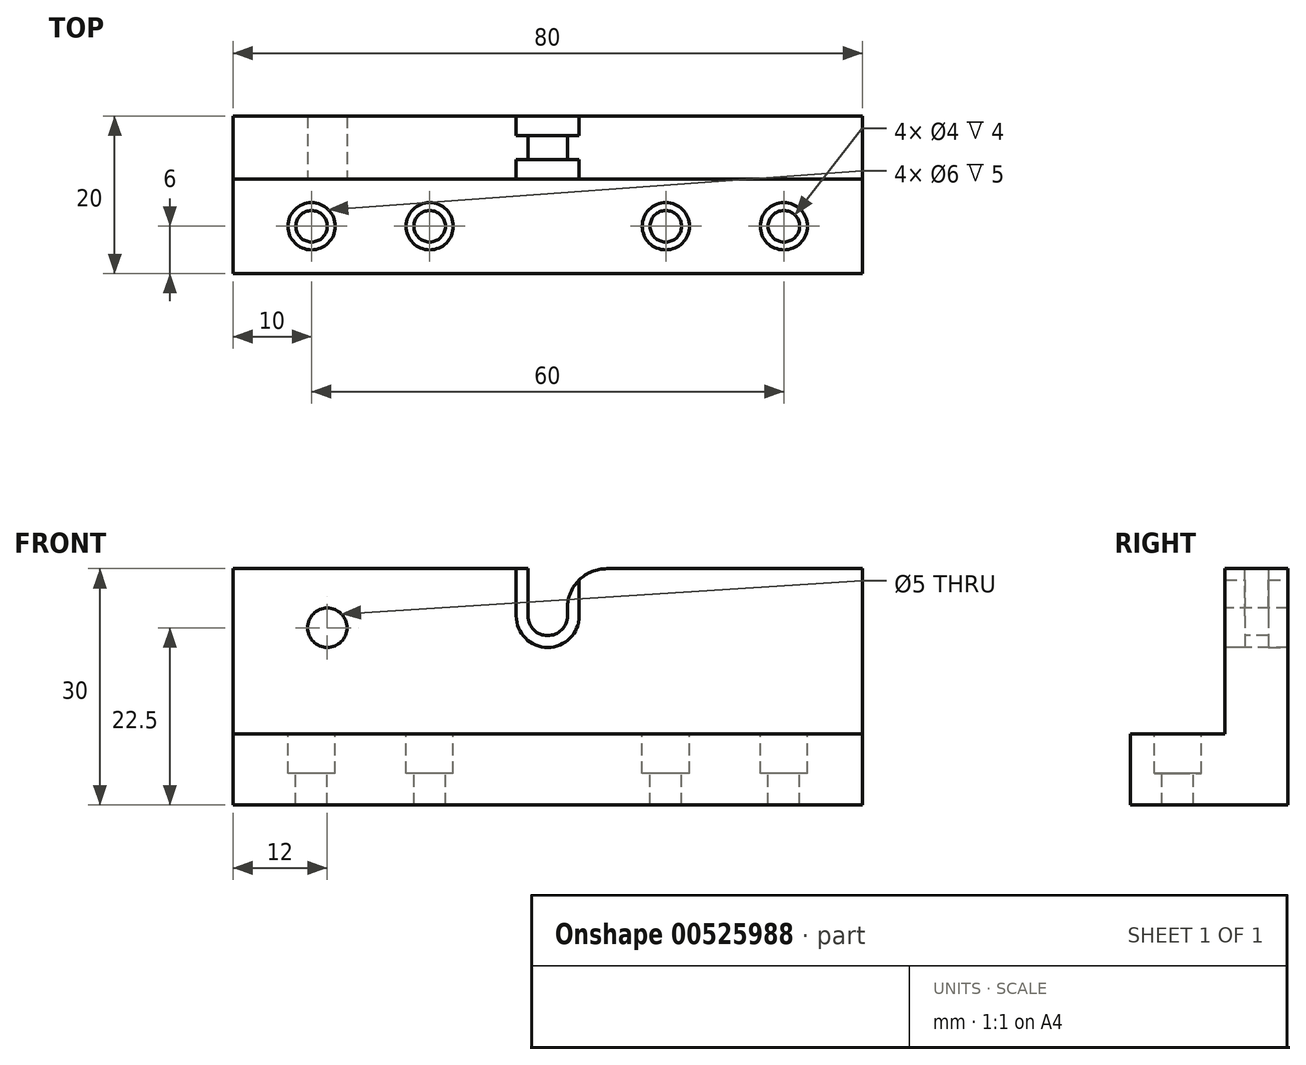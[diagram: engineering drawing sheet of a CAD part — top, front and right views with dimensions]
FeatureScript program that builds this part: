
annotation { "Feature Type Name" : "Feature", "Feature Type Description" : "" }
export const myFeature = defineFeature(function(context is Context, id is Id, definition is map)
    precondition{}
    {
        {
            var Q0;
            Q0=qCreatedBy(makeId("Top.planeOp"),FACE);
            var sketch = newSketch(context, id + "F0", { "sketchPlane" : qUnion([Q0])});
            skLineSegment(sketch, "E0.bottom", {"start": v(0, 0) * mm, "end": v(80, 0) * mm});
            skLineSegment(sketch, "E0.top", {"start": v(0, 8) * mm, "end": v(80, 8) * mm});
            skLineSegment(sketch, "E0.left", {"start": v(0, 0) * mm, "end": v(0, 8) * mm});
            skLineSegment(sketch, "E0.right", {"start": v(80, 0) * mm, "end": v(80, 8) * mm});
            skSolve(sketch);
        }
        {
            var Q0;
            Q0 = qSketchRegion(id + "F0", true);
            extrude(context, id + "F1", {"entities" : qUnion([Q0]), "depth" : 21 * mm, "offsetDistance" : 25 * mm});
        }
        {
            var Q0;
            Q0=makeQuery(id+"F1.opExtrude","SWEPT_FACE",FACE,{"disambiguationData":[OSD([sQuery(id+"F0.wireOp",EDGE,"E0.bottom")])]});
            var sketch = newSketch(context, id + "F2", { "sketchPlane" : qUnion([Q0])});
            skLineSegment(sketch, "E1", {"start": v(40, 21) * mm, "end": v(40, 0) * mm, "construction": true});
            skArc(sketch, "E2", {"start": v(37.5, 15) * mm, "mid": v(40, 12.5) * mm, "end": v(42.5, 15) * mm});
            skLineSegment(sketch, "E3", {"start": v(42.5, 15) * mm, "end": v(42.5, 21) * mm});
            skLineSegment(sketch, "E4", {"start": v(37.5, 15) * mm, "end": v(37.5, 21) * mm});
            skLineSegment(sketch, "E5", {"start": v(37.5, 21) * mm, "end": v(42.5, 21) * mm});
            skLineSegment(sketch, "E6", {"start": v(80, 15) * mm, "end": v(0, 15) * mm, "construction": true});
            skSolve(sketch);
        }
        {
            var Q0;
            Q0 = qSketchRegion(id + "F2", true);
            extrude(context, id + "F3", {"entities" : qUnion([Q0]), "operationType" : NewBodyOperationType.REMOVE, "oppositeDirection" : true, "depth" : 25 * mm, "offsetDistance" : 25 * mm});
        }
        {
            var Q0;
            Q0=makeQuery(id+"F1.opExtrude","SWEPT_FACE",FACE,{"disambiguationData":[OSD([sQuery(id+"F0.wireOp",EDGE,"E0.bottom")])]});
            var sketch = newSketch(context, id + "F4", { "sketchPlane" : qUnion([Q0])});
            skLineSegment(sketch, "E7.0", {"start": v(36, 15) * mm, "end": v(36, 15) * mm});
            skArc(sketch, "E7.1", {"start": v(36, 15) * mm, "mid": v(40, 11) * mm, "end": v(44, 15) * mm});
            skLineSegment(sketch, "E7.2", {"start": v(44, 15) * mm, "end": v(44, 15) * mm});
            skLineSegment(sketch, "E8", {"start": v(36, 15) * mm, "end": v(36, 21) * mm});
            skLineSegment(sketch, "E9", {"start": v(44, 15) * mm, "end": v(44, 21) * mm});
            skLineSegment(sketch, "E10", {"start": v(36, 21) * mm, "end": v(44, 21) * mm});
            skSolve(sketch);
        }
        {
            var Q0;
            Q0=makeQuery(id+"F4.imprint","IMPRINT",FACE,{"disambiguationData":[TD([[makeQuery(id+"F4.imprint","IMPRINT",EDGE,{"derivedFrom":sQuery(id+"F4.wireOp",EDGE,"E7.1")}),1.0]])]});
            extrude(context, id + "F5", {"entities" : qUnion([Q0]), "operationType" : NewBodyOperationType.REMOVE, "oppositeDirection" : true, "depth" : 2.5 * mm, "offsetDistance" : 25 * mm});
        }
        {
            var Q0;
            Q0=makeQuery(id+"F1.opExtrude","SWEPT_FACE",FACE,{"disambiguationData":[OSD([sQuery(id+"F0.wireOp",EDGE,"E0.top")])]});
            var sketch = newSketch(context, id + "F6", { "sketchPlane" : qUnion([Q0])});
            skLineSegment(sketch, "E11.0", {"start": v(-44, 15) * mm, "end": v(-44, 15) * mm});
            skArc(sketch, "E11.1", {"start": v(-44, 15) * mm, "mid": v(-40, 11) * mm, "end": v(-36, 15) * mm});
            skLineSegment(sketch, "E11.2", {"start": v(-36, 15) * mm, "end": v(-36, 15) * mm});
            skLineSegment(sketch, "E12", {"start": v(-36, 15) * mm, "end": v(-36, 21) * mm});
            skLineSegment(sketch, "E13", {"start": v(-36, 21) * mm, "end": v(-44, 21) * mm});
            skLineSegment(sketch, "E14", {"start": v(-44, 21) * mm, "end": v(-44, 15) * mm});
            skSolve(sketch);
        }
        {
            var Q0;
            Q0=makeQuery(id+"F6.imprint","IMPRINT",FACE,{"disambiguationData":[TD([[makeQuery(id+"F6.imprint","IMPRINT",EDGE,{"derivedFrom":sQuery(id+"F6.wireOp",EDGE,"E11.1")}),1.0]])]});
            extrude(context, id + "F7", {"entities" : qUnion([Q0]), "operationType" : NewBodyOperationType.REMOVE, "oppositeDirection" : true, "depth" : 2.5 * mm, "offsetDistance" : 25 * mm});
        }
        {
            var Q0;
            Q0=makeQuery(id+"F3.boolean.opBoolean","COPY",EDGE,{"derivedFrom":makeQuery(id+"F3.opExtrude","SWEPT_EDGE",EDGE,{"disambiguationData":[OSD([sQuery(id+"F0.wireOp",EDGE,"E0.bottom"),sQuery(id+"F2.wireOp",EDGE,"E3"),sQuery(id+"F2.wireOp",EDGE,"E5")])]})});
            var Q1;
            Q1=makeQuery(id+"F3.boolean.opBoolean","COPY",EDGE,{"derivedFrom":makeQuery(id+"F3.opExtrude","SWEPT_EDGE",EDGE,{"disambiguationData":[OSD([sQuery(id+"F0.wireOp",EDGE,"E0.bottom"),sQuery(id+"F2.wireOp",EDGE,"E4"),sQuery(id+"F2.wireOp",EDGE,"E5")])]})});
            fillet(context, id + "F8", {"entities" : qUnion([Q0, Q1]), "radius" : 5 * mm, "tangentPropagation" : true, "allowEdgeOverflow" : false});
        }
        {
            var Q0;
            Q0=makeQuery(id+"F1.opExtrude","CAP_FACE",FACE,{"disambiguationData":[OSD([sQuery(id+"F0.wireOp",EDGE,"E0.bottom"),sQuery(id+"F0.wireOp",EDGE,"E0.top"),sQuery(id+"F0.wireOp",EDGE,"E0.left"),sQuery(id+"F0.wireOp",EDGE,"E0.right")])],"isStart":true});
            var sketch = newSketch(context, id + "F9", { "sketchPlane" : qUnion([Q0])});
            skLineSegment(sketch, "E15.bottom", {"start": v(80, -8) * mm, "end": v(0, -8) * mm});
            skLineSegment(sketch, "E15.top", {"start": v(80, 12) * mm, "end": v(0, 12) * mm});
            skLineSegment(sketch, "E15.left", {"start": v(80, -8) * mm, "end": v(80, 12) * mm});
            skLineSegment(sketch, "E15.right", {"start": v(0, -8) * mm, "end": v(0, 12) * mm});
            skSolve(sketch);
        }
        {
            var Q0;
            Q0 = qSketchRegion(id + "F9", true);
            extrude(context, id + "F10", {"entities" : qUnion([Q0]), "operationType" : NewBodyOperationType.ADD, "depth" : 9 * mm, "offsetDistance" : 25 * mm});
        }
        {
            var Q0;
            Q0=makeQuery(id+"F10.opExtrude","CAP_FACE",FACE,{"disambiguationData":[OSD([sQuery(id+"F9.wireOp",EDGE,"E15.bottom"),sQuery(id+"F9.wireOp",EDGE,"E15.top"),sQuery(id+"F9.wireOp",EDGE,"E15.left"),sQuery(id+"F9.wireOp",EDGE,"E15.right")])],"isStart":true});
            var sketch = newSketch(context, id + "F11", { "sketchPlane" : qUnion([Q0])});
            skLineSegment(sketch, "E16", {"start": v(0, -6) * mm, "end": v(80, -6) * mm, "construction": true});
            skLineSegment(sketch, "E17", {"start": v(40, 0) * mm, "end": v(40, -12) * mm, "construction": true});
            skCircle(sketch, "E18", {"center": v(10, -6) * mm, "radius": 2 * mm});
            skCircle(sketch, "E19", {"center": v(25, -6) * mm, "radius": 2 * mm});
            skCircle(sketch, "E20", {"center": v(70, -6) * mm, "radius": 2 * mm});
            skCircle(sketch, "E21", {"center": v(55, -6) * mm, "radius": 2 * mm});
            skSolve(sketch);
        }
        {
            var Q0;
            Q0 = qSketchRegion(id + "F11", true);
            extrude(context, id + "F12", {"entities" : qUnion([Q0]), "operationType" : NewBodyOperationType.REMOVE, "oppositeDirection" : true, "depth" : 25 * mm, "offsetDistance" : 25 * mm});
        }
        {
            var Q0;
            Q0=makeQuery(id+"F10.opExtrude","CAP_FACE",FACE,{"disambiguationData":[OSD([sQuery(id+"F9.wireOp",EDGE,"E15.bottom"),sQuery(id+"F9.wireOp",EDGE,"E15.top"),sQuery(id+"F9.wireOp",EDGE,"E15.left"),sQuery(id+"F9.wireOp",EDGE,"E15.right")])],"isStart":true});
            var sketch = newSketch(context, id + "F13", { "sketchPlane" : qUnion([Q0])});
            skCircle(sketch, "E22", {"center": v(10, -6) * mm, "radius": 3 * mm});
            skCircle(sketch, "E23", {"center": v(25, -6) * mm, "radius": 3 * mm});
            skCircle(sketch, "E24", {"center": v(55, -6) * mm, "radius": 3 * mm});
            skCircle(sketch, "E25", {"center": v(70, -6) * mm, "radius": 3 * mm});
            skSolve(sketch);
        }
        {
            var Q0;
            Q0 = qSketchRegion(id + "F13", true);
            extrude(context, id + "F14", {"entities" : qUnion([Q0]), "operationType" : NewBodyOperationType.REMOVE, "oppositeDirection" : true, "depth" : 5 * mm, "offsetDistance" : 25 * mm});
        }
        {
            var Q0;
            Q0=makeQuery(id+"F1.opExtrude","SWEPT_FACE",FACE,{"disambiguationData":[OSD([sQuery(id+"F0.wireOp",EDGE,"E0.bottom")])]});
            var sketch = newSketch(context, id + "F15", { "sketchPlane" : qUnion([Q0])});
            skLineSegment(sketch, "E26", {"start": v(0, 13.5) * mm, "end": v(28.83, 13.5) * mm, "construction": true});
            skCircle(sketch, "E27", {"center": v(12, 13.5) * mm, "radius": 2.5 * mm});
            skSolve(sketch);
        }
        {
            var Q0;
            Q0 = qSketchRegion(id + "F15", true);
            extrude(context, id + "F16", {"entities" : qUnion([Q0]), "operationType" : NewBodyOperationType.REMOVE, "oppositeDirection" : true, "depth" : 25 * mm, "offsetDistance" : 25 * mm});
        }
    });
